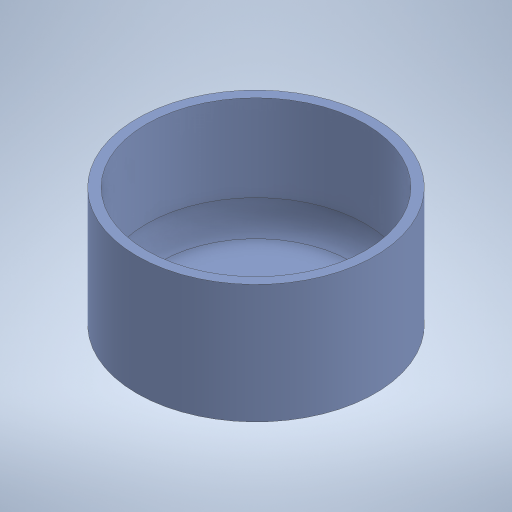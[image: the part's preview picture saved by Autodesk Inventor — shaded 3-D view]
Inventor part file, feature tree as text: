
AUTODESK INVENTOR PART (.ipt)
format: ipt  version: 2024 (Build 280153020, 153B)  size: 241,152 bytes
history: native  units: mm
features: sketch x2, revolve x1, extrude x1
ambient origin geometry x8: Origin, YZ Plane, XZ Plane, XY Plane, X Axis, Y Axis, Z Axis, Center Point
bodies: Solid1 (feature_tree)
feature tree (4):
  revolve  "Revolution1"  [1 undecoded]
  extrude  "Extrusion1"  Depth=25.0mm
  sketch  "Sketch1"  dims[d2=1.5mm d6=20.0mm]
  sketch  "Sketch3"  dims[d8=25.0mm d20=25.0mm d21=2.0mm d22=5.0mm d23=180.0deg d24=180.0deg d25=6.8mm d26=10.0mm d27=0.0mm d15=0.872665mm d16=0.872665mm]
note: 1 required parameter value undecoded (feature->parameter linkage not recoverable at this tier; creation-order binding heuristic only, values carry confidence <= 0.55)
